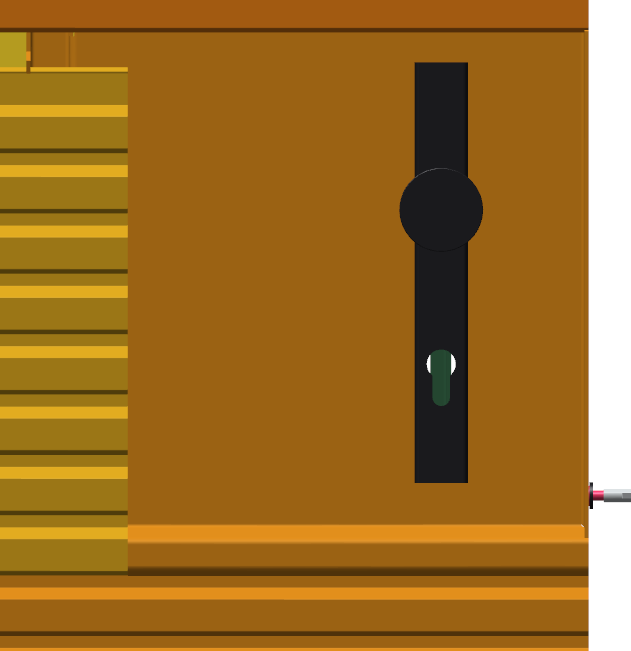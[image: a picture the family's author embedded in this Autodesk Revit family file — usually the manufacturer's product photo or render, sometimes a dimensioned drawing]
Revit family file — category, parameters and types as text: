
# Revit family: NLRS_31_DO_WB_HF66-66 enkele deur-AV_jazo_jazo
name_source: partatom
category: Doors
units: mm (PartAtom-declared; Revit-internal decimal feet)

## family parameters
Always vertical = Yes
Cut with Voids When Loaded = No
Host = Wall
OmniClass Number = 23.30.10.00
OmniClass Title = Doors
Room Calculation Point = No
Shared = No

## types (1)
- TYPE CATALOG
    Analytic Construction = <None>
    Assembly Code = 23.30.10.00
    Construction Type = Voor specificaties of mogelijkheden, neem contact op.
    Define Thermal Properties by = User Defined
    Description = HF66-66 enkele deur
    Function = Exterior
    Height = 2000 mm  [stored 6.56168 ft]
    JAZO_C_aluminium kozijn = No
    JAZO_C_calculatie_01 = 56 mm  [stored 0.183727 ft]
    JAZO_C_calculatie_02 = 532 mm
    JAZO_C_calculatie_03 = -64 mm
    JAZO_C_dagmaat breedte = 860 mm
    JAZO_C_dagmaat hoogte = 1860 mm
    JAZO_C_forster presto kozijn = Yes
    JAZO_C_materiaal aluminium kozijn = <By Category>
    JAZO_C_materiaal aluminium planken = <By Category>
    JAZO_C_materiaal beslag = <By Category>
    JAZO_C_materiaal forster presto deurprofiel = <By Category>
    JAZO_C_materiaal forster presto kozijn = <By Category>
    JAZO_C_materiaal forster presto sandwichpaneel = <By Category>
    JAZO_C_materiaal scharnier = <By Category>
    JAZO_C_materiaal schoep = <By Category>
    JAZO_C_niet ventilerend = Yes
    JAZO_C_opbouwrooster HF66 66 = Yes
    JAZO_C_paniekfunctie = No
    JAZO_C_ventilerend = No
    MAX HEIGHT = 3000 mm  [stored 9.84252 ft]
    MAX WIDTH = 1500 mm  [stored 4.92126 ft]
    MIN HEIGHT = 1850 mm  [stored 6.06955 ft]
    MIN WIDTH = 850 mm  [stored 2.78871 ft]
    Manufacturer = JAZO Zevenaar bv
    Model = HF66-66 enkele deur
    NLRS_C_aantal_01 = 2
    NLRS_C_aantal_02 = 8
    NLRS_C_brandwerend = No
    NLRS_C_breedte = 1000 mm  [stored 3.28084 ft]
    NLRS_C_breedte_01 = 1010 mm  [stored 3.31365 ft]
    NLRS_C_breedte_max = 1500 mm  [stored 4.92126 ft]
    NLRS_C_breedte_min = 850 mm  [stored 2.78871 ft]
    NLRS_C_content_datum gewijzigd = 7-11-2022
    NLRS_C_content_datum uitgifte = 17-8-2022
    NLRS_C_content_provider = JAZO Zevenaar bv
    NLRS_C_content_revit versie = REVIT 2020.2
    NLRS_C_content_versie = 2.5
    NLRS_C_diepte = 50 mm  [stored 0.164042 ft]
    NLRS_C_diepte_01 = 133 mm  [stored 0.436352 ft]
    NLRS_C_diepte_02 = 50 mm  [stored 0.164042 ft]
    NLRS_C_geluidwering Rw = Voor specificaties of mogelijkheden, neem contact op.
    NLRS_C_hoogte = 2000 mm  [stored 6.56168 ft]
    NLRS_C_hoogte_01 = 2010 mm  [stored 6.59449 ft]
    NLRS_C_hoogte_max = 3000 mm  [stored 9.84252 ft]
    NLRS_C_hoogte_min = 1850 mm  [stored 6.06955 ft]
    NLRS_C_inbraakwerend = No
    NLRS_C_lengte_01 = 119 mm  [stored 0.39042 ft]
    NLRS_C_lengte_02 = 532 mm
    NLRS_C_leverancier_adres = Handelsdwarsstraat 10
    NLRS_C_leverancier_bedrijfsnaam = JAZO Zevenaar bv
    NLRS_C_leverancier_plaats = Zevenaar
    NLRS_C_leverancier_postcode = 6905 DJ
    NLRS_C_leverancier_telefoonnummer = +31 316 - 59 29 11
    NLRS_C_leverancier_url = www.jazo.com
    NLRS_C_merk = Voor specificaties of mogelijkheden, neem contact op.
    NLRS_C_offset = 83 mm
    NLRS_C_offset_01 = 0 mm  [stored 0 ft]
    NLRS_C_offset_02 = 56 mm  [stored 0.183727 ft]
    NLRS_C_rookwerendheid = Voor specificaties of mogelijkheden, neem contact op.
    NLRS_C_stelruimte = 5 mm  [stored 0.0164042 ft]
    NLRS_C_vluchtroute = Voor specificaties of mogelijkheden, neem contact op.
    NLRS_C_weerstandsklasse = Voor specificaties of mogelijkheden, neem contact op.
    NLRS_C_zelfsluitend = No
    Negge = 83 mm
    Rough Height = 2010 mm  [stored 6.59449 ft]
    Rough Width = 1010 mm  [stored 3.31365 ft]
    Thickness = 50 mm  [stored 0.164042 ft]
    URL = www.jazo.com
    Wall Closure = By host
    Width = 1000 mm  [stored 3.28084 ft]

note: [stored X ft] marks values corroborated as IEEE doubles in the binary element streams (Revit-internal decimal feet)

## geometry (parser evidence)
native form markers: Sweep x38
no freeform markers — native parametric forms only
